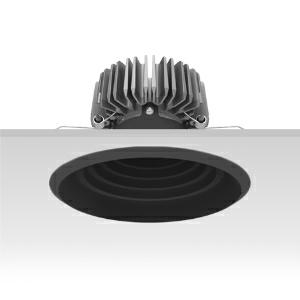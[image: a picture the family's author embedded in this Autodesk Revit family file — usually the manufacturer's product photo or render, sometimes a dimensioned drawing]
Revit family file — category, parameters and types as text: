
# Revit family: 3f_filippi_-_3f_reno_nero_ampio_3f_filippi_-_31525_-_3f_reno_200_bk_4000-930_wide
name_source: partatom
category: Lighting Fixtures
units: mm (PartAtom-declared; Revit-internal decimal feet)

## family parameters
Cut with Voids When Loaded = No
Host = Face
Light Source = No
Part Type = Normal
Room Calculation Point = No
Round Connector Dimension = Use Diameter
Shared = No

## types (1)
- 3F Filippi - 3F Reno Nero Ampio (1 x LED, 2732 lm, 43 W, 3000 K)
    Apparent Load = 43 VA
    Approval mark = CE
    CIE Flux Codes = 87 100 100 100 100
    Color Rendering = 90
    Color Temperature = 3000 K
    Control Gear = Electronic ballast
    Default Elevation = 1800 mm
    Description = ILLUMINOTECHNICAL
Luminous efficiency 100% (DLOR 100%, ULOR 0%).
Initial luminous flux of the luminaire 2732 lm.
Direct symmetric wide distribution.
Installation Interdistance Transv.D = 1.56 x hu - Long.D = 1.58 x hu.
Tabular UGR (CIE 117 - 4H-8H; S=0.25H; 70/50/20): RUG 19.9 - 19.9.
Beam angle: 84° - 84°.
Luminous efficacy 64 lm/W.
Lifetime (L90/B10): 30000 h. (tq+25°C)
Lifetime (L85/B10): 50000 h. (tq+25°C)
Lifetime (L70/B10): 80000 h. (tq+25°C)
Sudden decreased luminous flux after 50000 hours: 0% (C0).
Photobiological safety in compliance with IEC/TR 62778: RG1 low risk, (IEC 62471).
In compliance with IEC/EN 62722-2-1 - IEC/EN 62717 standards.

SOURCE
Compact LED module 4000/930.
Energy efficiency class (UE 2019/2020 - UE 2019/2015): F.
CIE 13.3 Colour rendering index: CRI >90 (R9 >50%).
IES TM-30 Fidelity Index: Rf = 92 Rg = 101.
CCT nominal colour temperature 3000 K.
Colour initial tolerance (MacAdam): SDCM 3.
Zhaga Book 3 compliant.

MECHANICAL
Passive heat dissipator in die-casting aluminium, oversized, for optimum thermal management of the LED module.
Parabolic element with graduated/concentric rings in black polycarbonate.
Transparent external lens with glossy and satin differentiated surfaces, with a cooling and anti-insect system in methacrylate (PMMA).
Fastening spring clips in stainless steel.
Dimensions: diameter 216 mm, height 142 mm. Weight 1.455 kg.
IP44 protection degree for exposed part, IP20 for recessed part.
Mechanical strength to impacts IK04 (0.5 joule).
Glow-wire test resistance 650°C.

ELECTRICAL
Wiring on a separate unit.
Halogen Free electronic wiring 230V-50/60Hz, power factor 0.95, THD <25%, constant output current, SELV, class II, 1 driver.
Power of the luminaire 43 W.
ENEC - CE.
SAFE FLICKER: PstLM=<1 and SVM=<0.4 (IEC TR 61547-1 and IEC TR 63158), to ensure a more comfortable and safe light.
Luminaire compliant with EN 60598-2-22 for power supply from a centralised emergency system CPSS (Central Power Supply System), not incorporated in the luminaire - high risk areas excluded. The default power and flux are 100% in AC and 100% in DC.
Ambient temperature from 0°C to +25°C.
Temperature class T6 max 85°C.
Relative humidity UR: <85%.

INSTALLATION
Pull-up recessed fitting.
False ceiling carving: 200 mm.
All accessories dedicated to this product are available on the Catalog and on our website www.3F-Filippi.com.

APPLICATIONS
Environments: architectural, commercial, exhibition areas, transit areas, corridors, shops, display windows, service areas.
In false ceilings with narrow voids.

WARNING
Luminaire designed for disposal/recycling at end-of-life.
Replaceable (LED only) light source by a professional. Replaceable control gear by a professional.
    Height = 0 mm  [stored 0 ft]
    Lamp = 1 x LED
    Lamp Light Flux = 2732 lm
    Lamp Power = 43 W
    Lamp count = 1
    Length = 216 mm
    Lifetime = 50000 h
    Luminous efficacy = 64 lm/W
    Manufacturer = 3F Filippi
    ModVariant = No
    Model = 3F Filippi - 31525 - 3F Reno 200 BK 4000-930 WIDE
    Mounting Place = Ceiling
    Mounting Type = Recessed
    Number of Poles = 1
    OnlyDefault = Yes
    Power Factor = 1
    Product Name = 3F Filippi - 3F Reno Nero Ampio
    Product group = recessed luminaire
    ProductGroupID = 4
    Protection Class = Protection class II
    Protection Degree = IP 20
    RLX_Detail_Level = 1
    RLX_Emergency_Light_Flux = 0 lm
    RLX_Emergency_Type = 0
    RLX_Emergency_Type_DB = No
    RlxData = <blob elided: 93309 chars, md5=050361bd>
    Socket = socket
    Standby Power = 0 W
    System Light Flux = 2732 lm
    System Power = 43 W
    Type Comments = Product without accessories
    Type Image = 3ffilippi_3f_reno_200_bk_2500_3000_4000.jpg
    URL = http://relux.com
    VarID = ---
    Voltage = 0 V
    Weight = 0.00 kg
    Width = 0 mm  [stored 0 ft]

note: [stored X ft] marks values corroborated as IEEE doubles in the binary element streams (Revit-internal decimal feet)

## geometry (parser evidence)
native form markers: Blend x4, Sweep x10
no freeform markers — native parametric forms only
